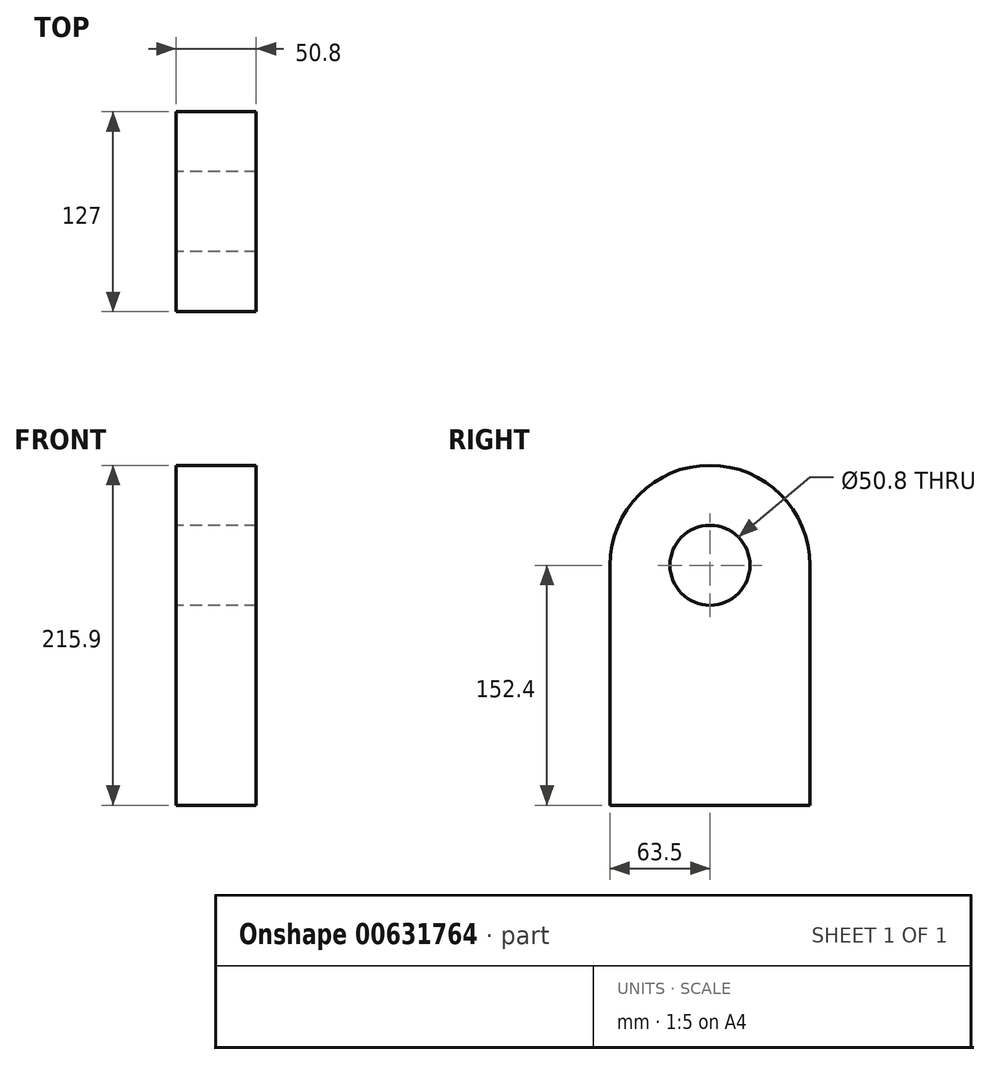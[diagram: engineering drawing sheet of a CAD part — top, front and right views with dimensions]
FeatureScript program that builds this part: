
annotation { "Feature Type Name" : "Feature", "Feature Type Description" : "" }
export const myFeature = defineFeature(function(context is Context, id is Id, definition is map)
    precondition{}
    {
        {
            var Q0;
            Q0=qCreatedBy(makeId("Right.planeOp"),FACE);
            var sketch = newSketch(context, id + "F0", { "sketchPlane" : qUnion([Q0])});
            skCircle(sketch, "E0", {"center": v(0, 0) * mm, "radius": 63.5 * mm});
            skLineSegment(sketch, "E1", {"start": v(-63.5, 0) * mm, "end": v(-63.5, -152.4) * mm});
            skLineSegment(sketch, "E2", {"start": v(63.5, 0) * mm, "end": v(63.5, -152.4) * mm});
            skLineSegment(sketch, "E3", {"start": v(-63.5, -152.4) * mm, "end": v(63.5, -152.4) * mm});
            skSolve(sketch);
        }
        {
            var Q0;
            Q0=qCreatedBy(makeId("Right.planeOp"),FACE);
            var sketch = newSketch(context, id + "F1", { "sketchPlane" : qUnion([Q0])});
            skCircle(sketch, "E4", {"center": v(0, 0) * mm, "radius": 25.4 * mm});
            skSolve(sketch);
        }
        {
            var Q0;
            Q0 = qSketchRegion(id + "F0", true);
            extrude(context, id + "F2", {"entities" : qUnion([Q0]), "endBound" : BoundingType.SYMMETRIC, "depth" : 50.8 * mm, "offsetDistance" : 25.4 * mm});
        }
        {
            var Q0;
            Q0 = qSketchRegion(id + "F1", true);
            extrude(context, id + "F3", {"entities" : qUnion([Q0]), "operationType" : NewBodyOperationType.REMOVE, "endBound" : BoundingType.SYMMETRIC, "depth" : 58.42 * mm, "offsetDistance" : 25.4 * mm});
        }
    });
